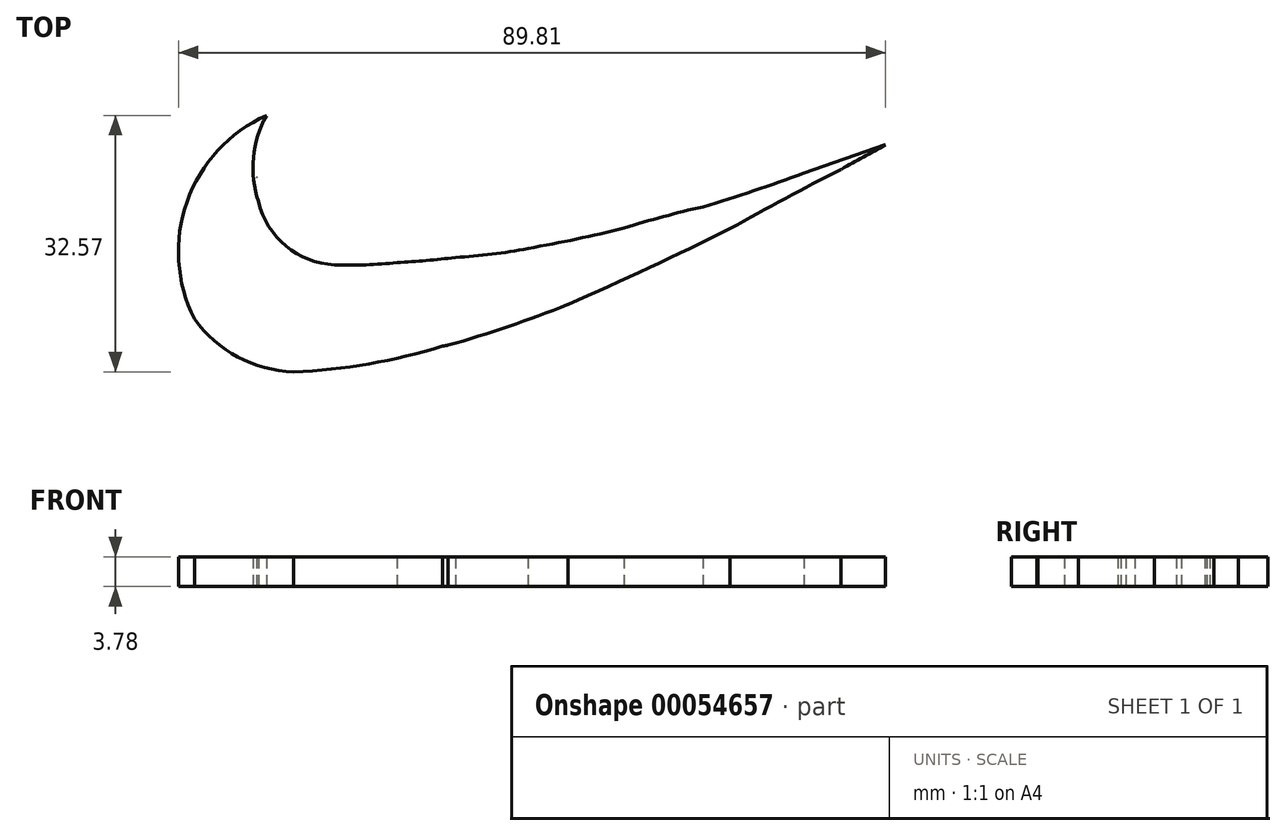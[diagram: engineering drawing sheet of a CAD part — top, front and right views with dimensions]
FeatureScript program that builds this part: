
annotation { "Feature Type Name" : "Feature", "Feature Type Description" : "" }
export const myFeature = defineFeature(function(context is Context, id is Id, definition is map)
    precondition{}
    {
        {
            var Q0;
            Q0=qCreatedBy(makeId("Top.planeOp"),FACE);
            var sketch = newSketch(context, id + "F0", { "sketchPlane" : qUnion([Q0])});
            skArc(sketch, "E0", {"start": v(-36.54, -21.98) * mm, "mid": v(-36.18, -21.92) * mm, "end": v(-35.82, -21.86) * mm});
            skArc(sketch, "E1", {"start": v(-34.92, -10.71) * mm, "mid": v(-30.27, -10.3) * mm, "end": v(-25.66, -9.57) * mm});
            skPoint(sketch, "E2.endSnap0", {"position": v(-41.8, -22.38) * mm});
            skArc(sketch, "E3", {"start": v(-25.66, -9.57) * mm, "mid": v(-19.55, -8.38) * mm, "end": v(-13.48, -7) * mm});
            skArc(sketch, "E4", {"start": v(14.1, 0.47) * mm, "mid": v(16.9, 2.03) * mm, "end": v(19.72, 3.6) * mm});
            skLineSegment(sketch, "E5", {"start": v(9.36, 0) * mm, "end": v(19.72, 3.6) * mm});
            skPoint(sketch, "E6.orphan", {"position": v(-50.32, -21.37) * mm});
            skArc(sketch, "E7", {"start": v(-60.17, -0.42) * mm, "mid": v(-60.18, -0.53) * mm, "end": v(-60.18, -0.64) * mm});
            skPoint(sketch, "E8.orphan", {"position": v(-55.92, 9.02) * mm});
            skPoint(sketch, "E9.orphan", {"position": v(-55.92, -12.2) * mm});
            skArc(sketch, "E10", {"start": v(-68.06, -18.53) * mm, "mid": v(-62.55, -23.35) * mm, "end": v(-55.48, -25.24) * mm});
            skPoint(sketch, "E10.endSnap0", {"position": v(-48.64, -22.95) * mm});
            skArc(sketch, "E11", {"start": v(-55.48, -25.24) * mm, "mid": v(-45.9, -24.24) * mm, "end": v(-36.54, -21.98) * mm});
            skPoint(sketch, "E12.end.orphan", {"position": v(-55.48, -22.45) * mm});
            skPoint(sketch, "E13.start.orphan", {"position": v(-46.63, -22.95) * mm});
            skPoint(sketch, "E14.orphan", {"position": v(-41.8, -10.7) * mm});
            skArc(sketch, "E15", {"start": v(-50.27, -11.65) * mm, "mid": v(-46.28, -11.65) * mm, "end": v(-42.3, -11.36) * mm});
            skArc(sketch, "E16", {"start": v(-42.3, -11.36) * mm, "mid": v(-38.6, -11.12) * mm, "end": v(-34.92, -10.71) * mm});
            skPoint(sketch, "E17.startSnap0", {"position": v(-30.27, -10.3) * mm});
            skArc(sketch, "E18", {"start": v(-3.44, -4.29) * mm, "mid": v(-8.5, -5.53) * mm, "end": v(-13.48, -7) * mm});
            skArc(sketch, "E19.trimOffspring", {"start": v(-3.44, -4.29) * mm, "mid": v(3, -2.25) * mm, "end": v(9.36, 0) * mm});
            skArc(sketch, "E20", {"start": v(-58.91, 7.33) * mm, "mid": v(-60.57, 1.95) * mm, "end": v(-59.92, -3.63) * mm});
            skArc(sketch, "E21", {"start": v(-58.91, 7.33) * mm, "mid": v(-69, -3.65) * mm, "end": v(-68.06, -18.53) * mm});
            skArc(sketch, "E22.trimOffspring", {"start": v(-59.92, -3.63) * mm, "mid": v(-56.44, -9.26) * mm, "end": v(-50.27, -11.65) * mm});
            skArc(sketch, "E23", {"start": v(-20.63, -16.72) * mm, "mid": v(-10.26, -12) * mm, "end": v(0, -7.07) * mm});
            skArc(sketch, "E24", {"start": v(14.1, 0.47) * mm, "mid": v(7, -3.22) * mm, "end": v(0, -7.07) * mm});
            skArc(sketch, "E25", {"start": v(-35.82, -21.86) * mm, "mid": v(-28.16, -19.48) * mm, "end": v(-20.63, -16.72) * mm});
            skPoint(sketch, "E26.end.orphan", {"position": v(-30.27, -20.48) * mm});
            skSolve(sketch);
        }
        {
            var Q0;
            Q0 = qSketchRegion(id + "F0", true);
            extrude(context, id + "F1", {"entities" : qUnion([Q0]), "depth" : 3.78 * mm});
        }
    });
